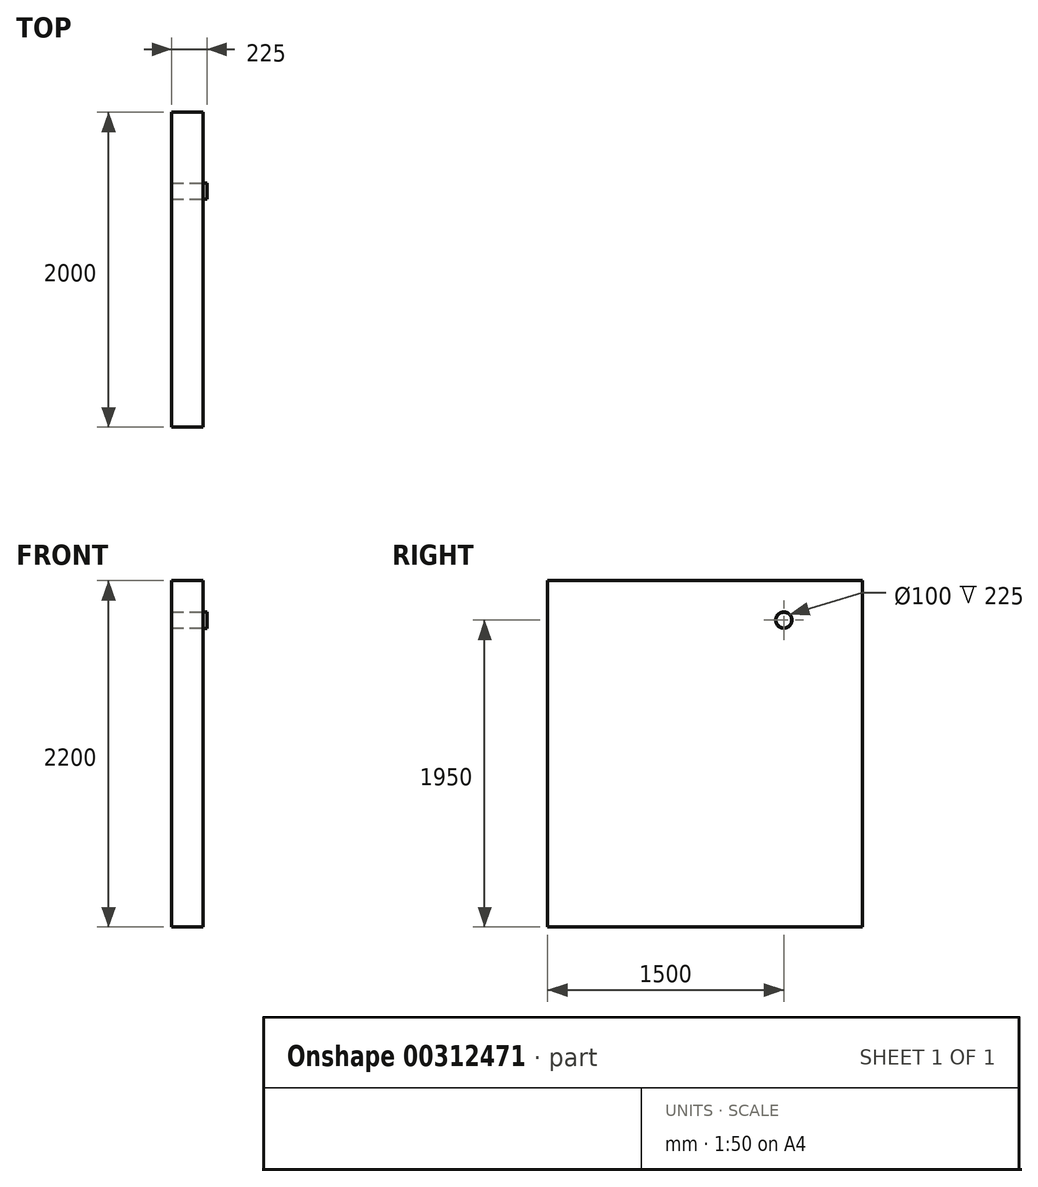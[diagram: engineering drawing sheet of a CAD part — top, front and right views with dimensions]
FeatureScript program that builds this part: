
annotation { "Feature Type Name" : "Feature", "Feature Type Description" : "" }
export const myFeature = defineFeature(function(context is Context, id is Id, definition is map)
    precondition{}
    {
        {
            var Q0;
            Q0=qCreatedBy(makeId("Right.planeOp"),FACE);
            var sketch = newSketch(context, id + "F0", { "sketchPlane" : qUnion([Q0])});
            skLineSegment(sketch, "E0.bottom", {"start": v(0, 0) * mm, "end": v(2000, 0) * mm});
            skLineSegment(sketch, "E0.top", {"start": v(0, 2200) * mm, "end": v(2000, 2200) * mm});
            skLineSegment(sketch, "E0.left", {"start": v(0, 0) * mm, "end": v(0, 2200) * mm});
            skLineSegment(sketch, "E0.right", {"start": v(2000, 0) * mm, "end": v(2000, 2200) * mm});
            skSolve(sketch);
        }
        {
            var Q0;
            Q0 = qSketchRegion(id + "F0", true);
            extrude(context, id + "F1", {"entities" : qUnion([Q0]), "depth" : 200 * mm});
        }
        {
            var Q0;
            Q0=makeQuery(id+"F1.opExtrude","CAP_FACE",FACE,{"disambiguationData":[OSD([sQuery(id+"F0.wireOp",EDGE,"E0.bottom"),sQuery(id+"F0.wireOp",EDGE,"E0.top"),sQuery(id+"F0.wireOp",EDGE,"E0.left"),sQuery(id+"F0.wireOp",EDGE,"E0.right")])],"isStart":false});
            var sketch = newSketch(context, id + "F2", { "sketchPlane" : qUnion([Q0])});
            skPoint(sketch, "E1", {"position": v(1500, 1950) * mm});
            skSolve(sketch);
        }
        {
            var Q0;
            Q0=sQuery(id+"F2.wireOp",VERTEX,"E1");
            var Q1;
            Q1=makeQuery(id+"F1.opExtrude","SWEPT_BODY",BODY,{"disambiguationData":[OSD([sQuery(id+"F0.wireOp",EDGE,"E0.bottom"),sQuery(id+"F0.wireOp",EDGE,"E0.top"),sQuery(id+"F0.wireOp",EDGE,"E0.left"),sQuery(id+"F0.wireOp",EDGE,"E0.right")])]});
            hole(context, id + "F3", {"style" : HoleStyle.SIMPLE, "endStyle" : HoleEndStyle.THROUGH, "holeDiameter" : 100 * mm, "tappedDepth" : 12 * mm, "tapClearance" : 3, "locations" : qUnion([Q0]), "scope" : qUnion([Q1])});
        }
        {
            var Q0;
            Q0=makeQuery(id+"F1.opExtrude","CAP_FACE",FACE,{"disambiguationData":[OSD([sQuery(id+"F0.wireOp",EDGE,"E0.bottom"),sQuery(id+"F0.wireOp",EDGE,"E0.top"),sQuery(id+"F0.wireOp",EDGE,"E0.left"),sQuery(id+"F0.wireOp",EDGE,"E0.right")])],"isStart":false});
            var sketch = newSketch(context, id + "F4", { "sketchPlane" : qUnion([Q0])});
            skCircle(sketch, "E2.0", {"center": v(1500, 1950) * mm, "radius": 50 * mm});
            skCircle(sketch, "E3.0", {"center": v(1500, 1950) * mm, "radius": 52 * mm});
            skSolve(sketch);
        }
        {
            var Q0;
            Q0 = qSketchRegion(id + "F4", true);
            extrude(context, id + "F5", {"entities" : qUnion([Q0]), "operationType" : NewBodyOperationType.ADD, "depth" : 25 * mm});
        }
    });
